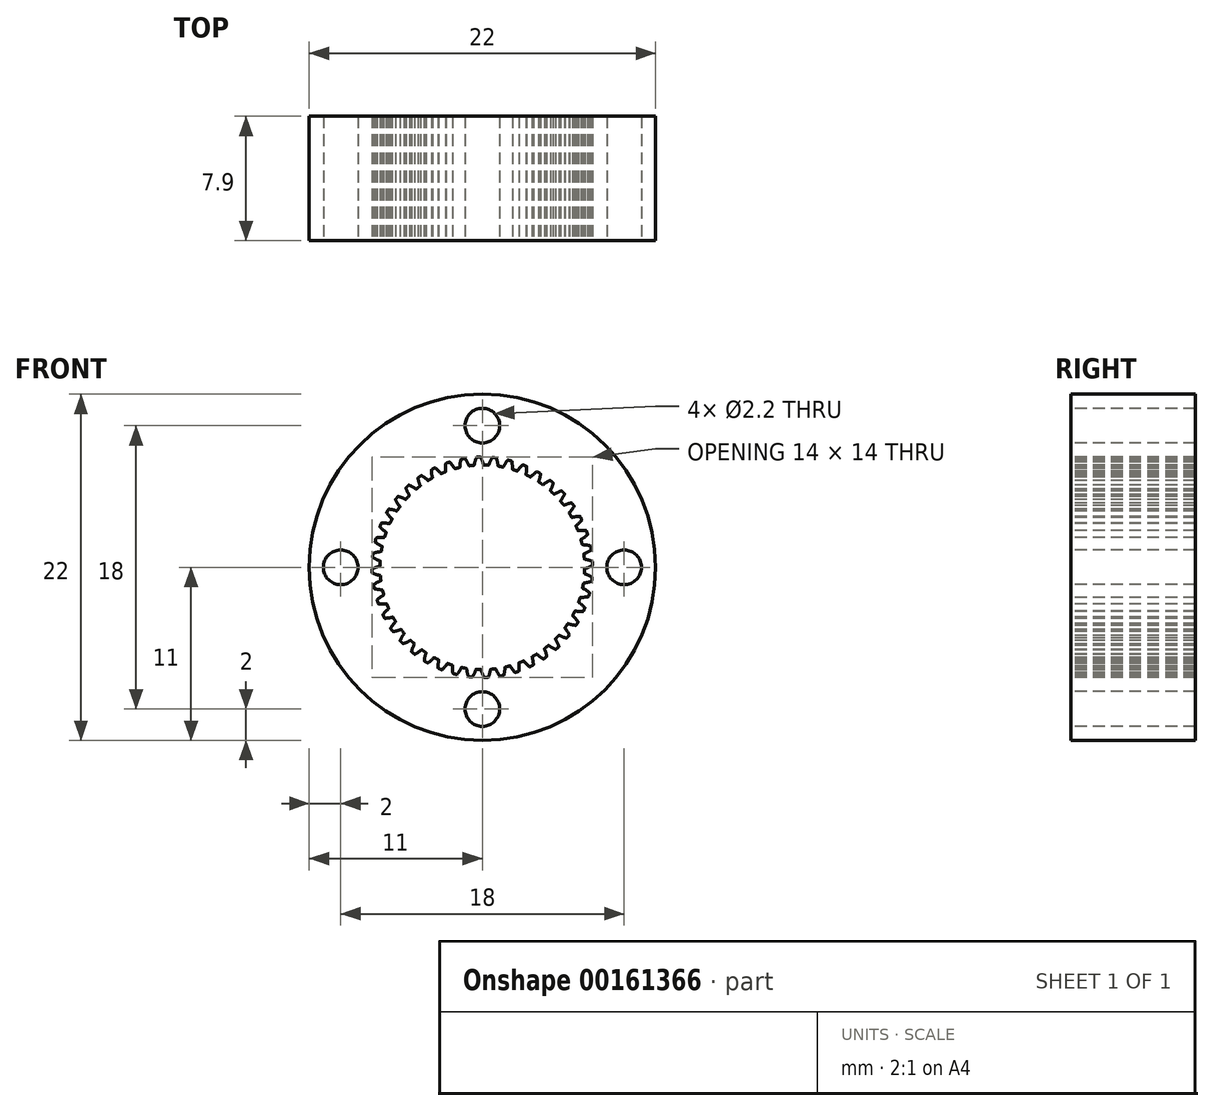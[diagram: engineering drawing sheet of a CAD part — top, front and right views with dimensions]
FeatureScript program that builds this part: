
annotation { "Feature Type Name" : "Feature", "Feature Type Description" : "" }
export const myFeature = defineFeature(function(context is Context, id is Id, definition is map)
    precondition{}
    {
        {
            var Q0;
            Q0=qCreatedBy(makeId("Front.planeOp"),FACE);
            var sketch = newSketch(context, id + "F0", { "sketchPlane" : qUnion([Q0])});
            skCircle(sketch, "E0", {"center": v(0, 0) * mm, "radius": 11 * mm});
            skSolve(sketch);
        }
        {
            var Q0;
            Q0=qSketchRegion(id+"F0",true);
            var Q1;
            Q1=makeQuery(id+"F0.imprint","IMPRINT",FACE,{"disambiguationData":[TD([[makeQuery(id+"F0.imprint","IMPRINT",EDGE,{"derivedFrom":sQuery(id+"F0.wireOp",EDGE,"E0")}),1.0]])]});
            extrude(context, id + "F1", {"entities" : qUnion([Q0, Q1]), "depth" : 7.9 * mm});
        }
        {
            var Q0;
            Q0=makeQuery(id+"F1.opExtrude","CAP_FACE",FACE,{"disambiguationData":[OSD([sQuery(id+"F0.wireOp",EDGE,"E0"),sQuery(id+"F0.wireOp",EDGE,"2902f3af-6cdb-4536-80c8-8346aa25ecb7")])],"isStart":false});
            var sketch = newSketch(context, id + "F2", { "sketchPlane" : qUnion([Q0])});
            skLineSegment(sketch, "E1", {"start": v(0, 27.51) * mm, "end": v(0, -34.9) * mm, "construction": true});
            skCircle(sketch, "E2", {"center": v(0, 9) * mm, "radius": 1.1 * mm});
            skCircle(sketch, "E3.1.0", {"center": v(-9, 0) * mm, "radius": 1.1 * mm});
            skCircle(sketch, "E3.2.0", {"center": v(0, -9) * mm, "radius": 1.1 * mm});
            skCircle(sketch, "E3.3.0", {"center": v(9, 0) * mm, "radius": 1.1 * mm});
            skPoint(sketch, "E3.center", {"position": v(0, 0) * mm});
            skSolve(sketch);
        }
        {
            var Q0;
            Q0=qSketchRegion(id+"F2",true);
            extrude(context, id + "F3", {"entities" : qUnion([Q0]), "operationType" : NewBodyOperationType.REMOVE, "endBound" : BoundingType.THROUGH_ALL, "oppositeDirection" : true, "depth" : 25 * mm});
        }
        {
            var Q0;
            Q0=makeQuery(id+"F1.opExtrude","CAP_FACE",FACE,{"disambiguationData":[OSD([sQuery(id+"F0.wireOp",EDGE,"E0")])],"isStart":false});
            var sketch = newSketch(context, id + "F4", { "sketchPlane" : qUnion([Q0])});
            skCircle(sketch, "E4", {"center": v(0, 0) * mm, "radius": 7 * mm, "construction": true});
            skCircle(sketch, "E5", {"center": v(0, 0) * mm, "radius": 6.75 * mm, "construction": true});
            skCircle(sketch, "E6", {"center": v(0, 0) * mm, "radius": 6.5 * mm, "construction": true});
            skLineSegment(sketch, "E7", {"start": v(0, 0) * mm, "end": v(0, 20.22) * mm, "construction": true});
            skLineSegment(sketch, "E8", {"start": v(0, 0) * mm, "end": v(-0.7, 20.22) * mm, "construction": true});
            skLineSegment(sketch, "E9", {"start": v(0, 6.75) * mm, "end": v(-8.2, 6.75) * mm, "construction": true});
            skLineSegment(sketch, "E10", {"start": v(0, 6.75) * mm, "end": v(-7.4, 4.05) * mm, "construction": true});
            skCircle(sketch, "E11", {"center": v(0, 6.75) * mm, "radius": 2.07 * mm, "construction": true});
            skCircle(sketch, "E12", {"center": v(-1.95, 6.04) * mm, "radius": 2.07 * mm, "construction": true});
            skArc(sketch, "E13", {"start": v(-0.1, 7) * mm, "mid": v(0, 6.76) * mm, "end": v(0.07, 6.5) * mm, "construction": true});
            skArc(sketch, "E14.MirrorCS", {"start": v(-0.37, 7) * mm, "mid": v(-0.46, 6.74) * mm, "end": v(-0.52, 6.48) * mm, "construction": true});
            skArc(sketch, "E15", {"start": v(-0.37, 6.98) * mm, "mid": v(-0.46, 6.74) * mm, "end": v(-0.52, 6.49) * mm});
            skArc(sketch, "E16", {"start": v(-0.36, 7) * mm, "mid": v(-0.24, 7) * mm, "end": v(-0.12, 7) * mm});
            skArc(sketch, "E17", {"start": v(-0.1, 7) * mm, "mid": v(0, 6.76) * mm, "end": v(0.07, 6.5) * mm});
            skArc(sketch, "E18", {"start": v(-0.53, 6.48) * mm, "mid": v(0.22, -6.5) * mm, "end": v(0.08, 6.5) * mm});
            skPoint(sketch, "E19.visualSharp", {"position": v(-0.52, 6.48) * mm});
            skArc(sketch, "E19.filletArc", {"start": v(-0.53, 6.48) * mm, "mid": v(-0.52, 6.48) * mm, "end": v(-0.52, 6.49) * mm});
            skPoint(sketch, "E20.visualSharp", {"position": v(-0.37, 7) * mm});
            skArc(sketch, "E20.filletArc", {"start": v(-0.36, 7) * mm, "mid": v(-0.37, 6.99) * mm, "end": v(-0.37, 6.98) * mm});
            skPoint(sketch, "E21.visualSharp", {"position": v(-0.1, 7) * mm});
            skArc(sketch, "E21.filletArc", {"start": v(-0.1, 7) * mm, "mid": v(-0.11, 7) * mm, "end": v(-0.12, 7) * mm});
            skPoint(sketch, "E22.visualSharp", {"position": v(0.07, 6.5) * mm});
            skArc(sketch, "E22.filletArc", {"start": v(0.07, 6.5) * mm, "mid": v(0.08, 6.5) * mm, "end": v(0.08, 6.5) * mm});
            skArc(sketch, "E23.1.0", {"start": v(-1.44, 6.34) * mm, "mid": v(-1.44, 6.34) * mm, "end": v(-1.43, 6.35) * mm});
            skArc(sketch, "E23.1.1", {"start": v(-1.36, 6.86) * mm, "mid": v(-1.41, 6.6) * mm, "end": v(-1.43, 6.35) * mm});
            skArc(sketch, "E23.1.2", {"start": v(-1.35, 6.87) * mm, "mid": v(-1.36, 6.87) * mm, "end": v(-1.36, 6.86) * mm});
            skArc(sketch, "E23.1.3", {"start": v(-1.35, 6.87) * mm, "mid": v(-1.23, 6.9) * mm, "end": v(-1.11, 6.91) * mm});
            skArc(sketch, "E23.1.4", {"start": v(-1.1, 6.9) * mm, "mid": v(-1.1, 6.91) * mm, "end": v(-1.11, 6.91) * mm});
            skArc(sketch, "E23.1.5", {"start": v(-1.1, 6.9) * mm, "mid": v(-0.96, 6.69) * mm, "end": v(-0.86, 6.45) * mm});
            skArc(sketch, "E23.1.6", {"start": v(-0.86, 6.45) * mm, "mid": v(-0.85, 6.45) * mm, "end": v(-0.84, 6.45) * mm});
            skArc(sketch, "E23.2.0", {"start": v(-2.33, 6.07) * mm, "mid": v(-2.32, 6.07) * mm, "end": v(-2.32, 6.08) * mm});
            skArc(sketch, "E23.2.1", {"start": v(-2.32, 6.6) * mm, "mid": v(-2.34, 6.34) * mm, "end": v(-2.32, 6.08) * mm});
            skArc(sketch, "E23.2.2", {"start": v(-2.31, 6.6) * mm, "mid": v(-2.32, 6.6) * mm, "end": v(-2.32, 6.6) * mm});
            skArc(sketch, "E23.2.3", {"start": v(-2.31, 6.6) * mm, "mid": v(-2.2, 6.65) * mm, "end": v(-2.09, 6.68) * mm});
            skArc(sketch, "E23.2.4", {"start": v(-2.07, 6.68) * mm, "mid": v(-2.08, 6.68) * mm, "end": v(-2.09, 6.68) * mm});
            skArc(sketch, "E23.2.5", {"start": v(-2.07, 6.68) * mm, "mid": v(-1.9, 6.48) * mm, "end": v(-1.77, 6.27) * mm});
            skArc(sketch, "E23.2.6", {"start": v(-1.77, 6.27) * mm, "mid": v(-1.76, 6.26) * mm, "end": v(-1.75, 6.26) * mm});
            skArc(sketch, "E23.3.0", {"start": v(-3.17, 5.67) * mm, "mid": v(-3.17, 5.68) * mm, "end": v(-3.16, 5.69) * mm});
            skArc(sketch, "E23.3.1", {"start": v(-3.24, 6.2) * mm, "mid": v(-3.22, 5.94) * mm, "end": v(-3.16, 5.69) * mm});
            skArc(sketch, "E23.3.2", {"start": v(-3.23, 6.2) * mm, "mid": v(-3.24, 6.2) * mm, "end": v(-3.24, 6.2) * mm});
            skArc(sketch, "E23.3.3", {"start": v(-3.23, 6.2) * mm, "mid": v(-3.12, 6.26) * mm, "end": v(-3.01, 6.32) * mm});
            skArc(sketch, "E23.3.4", {"start": v(-3, 6.32) * mm, "mid": v(-3, 6.32) * mm, "end": v(-3.01, 6.32) * mm});
            skArc(sketch, "E23.3.5", {"start": v(-3, 6.32) * mm, "mid": v(-2.8, 6.14) * mm, "end": v(-2.64, 5.95) * mm});
            skArc(sketch, "E23.3.6", {"start": v(-2.64, 5.95) * mm, "mid": v(-2.63, 5.95) * mm, "end": v(-2.62, 5.95) * mm});
            skArc(sketch, "E23.4.0", {"start": v(-3.95, 5.16) * mm, "mid": v(-3.94, 5.17) * mm, "end": v(-3.94, 5.18) * mm});
            skArc(sketch, "E23.4.1", {"start": v(-4.09, 5.67) * mm, "mid": v(-4.03, 5.42) * mm, "end": v(-3.94, 5.18) * mm});
            skArc(sketch, "E23.4.2", {"start": v(-4.08, 5.69) * mm, "mid": v(-4.09, 5.68) * mm, "end": v(-4.09, 5.67) * mm});
            skArc(sketch, "E23.4.3", {"start": v(-4.08, 5.69) * mm, "mid": v(-3.98, 5.76) * mm, "end": v(-3.88, 5.82) * mm});
            skArc(sketch, "E23.4.4", {"start": v(-3.87, 5.82) * mm, "mid": v(-3.88, 5.83) * mm, "end": v(-3.88, 5.82) * mm});
            skArc(sketch, "E23.4.5", {"start": v(-3.87, 5.82) * mm, "mid": v(-3.65, 5.68) * mm, "end": v(-3.46, 5.52) * mm});
            skArc(sketch, "E23.4.6", {"start": v(-3.46, 5.52) * mm, "mid": v(-3.45, 5.51) * mm, "end": v(-3.44, 5.51) * mm});
            skArc(sketch, "E23.5.0", {"start": v(-4.64, 4.55) * mm, "mid": v(-4.64, 4.56) * mm, "end": v(-4.64, 4.57) * mm});
            skArc(sketch, "E23.5.1", {"start": v(-4.85, 5.03) * mm, "mid": v(-4.76, 4.8) * mm, "end": v(-4.64, 4.57) * mm});
            skArc(sketch, "E23.5.2", {"start": v(-4.85, 5.05) * mm, "mid": v(-4.85, 5.04) * mm, "end": v(-4.85, 5.03) * mm});
            skArc(sketch, "E23.5.3", {"start": v(-4.85, 5.05) * mm, "mid": v(-4.76, 5.13) * mm, "end": v(-4.67, 5.21) * mm});
            skArc(sketch, "E23.5.4", {"start": v(-4.66, 5.21) * mm, "mid": v(-4.67, 5.22) * mm, "end": v(-4.67, 5.21) * mm});
            skArc(sketch, "E23.5.5", {"start": v(-4.66, 5.21) * mm, "mid": v(-4.43, 5.1) * mm, "end": v(-4.2, 4.97) * mm});
            skArc(sketch, "E23.5.6", {"start": v(-4.2, 4.97) * mm, "mid": v(-4.2, 4.96) * mm, "end": v(-4.2, 4.97) * mm});
            skArc(sketch, "E23.6.0", {"start": v(-5.24, 3.84) * mm, "mid": v(-5.24, 3.85) * mm, "end": v(-5.24, 3.86) * mm});
            skArc(sketch, "E23.6.1", {"start": v(-5.52, 4.3) * mm, "mid": v(-5.4, 4.07) * mm, "end": v(-5.24, 3.86) * mm});
            skArc(sketch, "E23.6.2", {"start": v(-5.52, 4.3) * mm, "mid": v(-5.52, 4.3) * mm, "end": v(-5.52, 4.3) * mm});
            skArc(sketch, "E23.6.3", {"start": v(-5.52, 4.3) * mm, "mid": v(-5.44, 4.4) * mm, "end": v(-5.37, 4.5) * mm});
            skArc(sketch, "E23.6.4", {"start": v(-5.35, 4.5) * mm, "mid": v(-5.36, 4.5) * mm, "end": v(-5.37, 4.5) * mm});
            skArc(sketch, "E23.6.5", {"start": v(-5.35, 4.5) * mm, "mid": v(-5.1, 4.42) * mm, "end": v(-4.87, 4.32) * mm});
            skArc(sketch, "E23.6.6", {"start": v(-4.87, 4.32) * mm, "mid": v(-4.86, 4.32) * mm, "end": v(-4.86, 4.32) * mm});
            skArc(sketch, "E23.7.0", {"start": v(-5.74, 3.06) * mm, "mid": v(-5.73, 3.07) * mm, "end": v(-5.74, 3.08) * mm});
            skArc(sketch, "E23.7.1", {"start": v(-6.08, 3.46) * mm, "mid": v(-5.92, 3.26) * mm, "end": v(-5.74, 3.08) * mm});
            skArc(sketch, "E23.7.2", {"start": v(-6.08, 3.48) * mm, "mid": v(-6.08, 3.47) * mm, "end": v(-6.08, 3.46) * mm});
            skArc(sketch, "E23.7.3", {"start": v(-6.08, 3.48) * mm, "mid": v(-6.01, 3.58) * mm, "end": v(-5.95, 3.68) * mm});
            skArc(sketch, "E23.7.4", {"start": v(-5.94, 3.7) * mm, "mid": v(-5.95, 3.69) * mm, "end": v(-5.95, 3.68) * mm});
            skArc(sketch, "E23.7.5", {"start": v(-5.94, 3.7) * mm, "mid": v(-5.69, 3.65) * mm, "end": v(-5.44, 3.58) * mm});
            skArc(sketch, "E23.7.6", {"start": v(-5.44, 3.58) * mm, "mid": v(-5.43, 3.58) * mm, "end": v(-5.42, 3.58) * mm});
            skArc(sketch, "E23.8.0", {"start": v(-6.11, 2.21) * mm, "mid": v(-6.11, 2.22) * mm, "end": v(-6.12, 2.23) * mm});
            skArc(sketch, "E23.8.1", {"start": v(-6.5, 2.56) * mm, "mid": v(-6.32, 2.38) * mm, "end": v(-6.12, 2.23) * mm});
            skArc(sketch, "E23.8.2", {"start": v(-6.5, 2.58) * mm, "mid": v(-6.5, 2.57) * mm, "end": v(-6.5, 2.56) * mm});
            skArc(sketch, "E23.8.3", {"start": v(-6.5, 2.58) * mm, "mid": v(-6.46, 2.69) * mm, "end": v(-6.42, 2.8) * mm});
            skArc(sketch, "E23.8.4", {"start": v(-6.4, 2.8) * mm, "mid": v(-6.41, 2.8) * mm, "end": v(-6.42, 2.8) * mm});
            skArc(sketch, "E23.8.5", {"start": v(-6.4, 2.8) * mm, "mid": v(-6.15, 2.8) * mm, "end": v(-5.9, 2.77) * mm});
            skArc(sketch, "E23.8.6", {"start": v(-5.9, 2.77) * mm, "mid": v(-5.88, 2.77) * mm, "end": v(-5.88, 2.78) * mm});
            skArc(sketch, "E23.9.0", {"start": v(-6.36, 1.32) * mm, "mid": v(-6.37, 1.33) * mm, "end": v(-6.37, 1.33) * mm});
            skArc(sketch, "E23.9.1", {"start": v(-6.8, 1.61) * mm, "mid": v(-6.6, 1.46) * mm, "end": v(-6.37, 1.33) * mm});
            skArc(sketch, "E23.9.2", {"start": v(-6.8, 1.62) * mm, "mid": v(-6.8, 1.62) * mm, "end": v(-6.8, 1.61) * mm});
            skArc(sketch, "E23.9.3", {"start": v(-6.8, 1.62) * mm, "mid": v(-6.78, 1.74) * mm, "end": v(-6.75, 1.86) * mm});
            skArc(sketch, "E23.9.4", {"start": v(-6.74, 1.87) * mm, "mid": v(-6.74, 1.86) * mm, "end": v(-6.75, 1.86) * mm});
            skArc(sketch, "E23.9.5", {"start": v(-6.74, 1.87) * mm, "mid": v(-6.48, 1.9) * mm, "end": v(-6.23, 1.9) * mm});
            skArc(sketch, "E23.9.6", {"start": v(-6.23, 1.9) * mm, "mid": v(-6.22, 1.9) * mm, "end": v(-6.21, 1.91) * mm});
            skArc(sketch, "E23.10.0", {"start": v(-6.49, 0.4) * mm, "mid": v(-6.5, 0.4) * mm, "end": v(-6.5, 0.41) * mm});
            skArc(sketch, "E23.10.1", {"start": v(-6.96, 0.63) * mm, "mid": v(-6.74, 0.5) * mm, "end": v(-6.5, 0.41) * mm});
            skArc(sketch, "E23.10.2", {"start": v(-6.97, 0.64) * mm, "mid": v(-6.97, 0.63) * mm, "end": v(-6.96, 0.63) * mm});
            skArc(sketch, "E23.10.3", {"start": v(-6.97, 0.64) * mm, "mid": v(-6.96, 0.76) * mm, "end": v(-6.94, 0.88) * mm});
            skArc(sketch, "E23.10.4", {"start": v(-6.94, 0.9) * mm, "mid": v(-6.94, 0.89) * mm, "end": v(-6.94, 0.88) * mm});
            skArc(sketch, "E23.10.5", {"start": v(-6.94, 0.9) * mm, "mid": v(-6.69, 0.96) * mm, "end": v(-6.43, 1) * mm});
            skArc(sketch, "E23.10.6", {"start": v(-6.43, 1) * mm, "mid": v(-6.43, 1) * mm, "end": v(-6.42, 1) * mm});
            skArc(sketch, "E23.11.0", {"start": v(-6.48, -0.53) * mm, "mid": v(-6.48, -0.52) * mm, "end": v(-6.49, -0.52) * mm});
            skArc(sketch, "E23.11.1", {"start": v(-6.98, -0.37) * mm, "mid": v(-6.74, -0.46) * mm, "end": v(-6.49, -0.52) * mm});
            skArc(sketch, "E23.11.2", {"start": v(-7, -0.36) * mm, "mid": v(-6.99, -0.37) * mm, "end": v(-6.98, -0.37) * mm});
            skArc(sketch, "E23.11.3", {"start": v(-7, -0.36) * mm, "mid": v(-7, -0.24) * mm, "end": v(-7, -0.12) * mm});
            skArc(sketch, "E23.11.4", {"start": v(-7, -0.1) * mm, "mid": v(-7, -0.11) * mm, "end": v(-7, -0.12) * mm});
            skArc(sketch, "E23.11.5", {"start": v(-7, -0.1) * mm, "mid": v(-6.76, 0) * mm, "end": v(-6.5, 0.07) * mm});
            skArc(sketch, "E23.11.6", {"start": v(-6.5, 0.07) * mm, "mid": v(-6.5, 0.08) * mm, "end": v(-6.5, 0.08) * mm});
            skArc(sketch, "E23.12.0", {"start": v(-6.34, -1.44) * mm, "mid": v(-6.34, -1.44) * mm, "end": v(-6.35, -1.43) * mm});
            skArc(sketch, "E23.12.1", {"start": v(-6.86, -1.36) * mm, "mid": v(-6.6, -1.41) * mm, "end": v(-6.35, -1.43) * mm});
            skArc(sketch, "E23.12.2", {"start": v(-6.87, -1.35) * mm, "mid": v(-6.87, -1.36) * mm, "end": v(-6.86, -1.36) * mm});
            skArc(sketch, "E23.12.3", {"start": v(-6.87, -1.35) * mm, "mid": v(-6.9, -1.23) * mm, "end": v(-6.91, -1.11) * mm});
            skArc(sketch, "E23.12.4", {"start": v(-6.9, -1.1) * mm, "mid": v(-6.91, -1.1) * mm, "end": v(-6.91, -1.11) * mm});
            skArc(sketch, "E23.12.5", {"start": v(-6.9, -1.1) * mm, "mid": v(-6.69, -0.96) * mm, "end": v(-6.45, -0.86) * mm});
            skArc(sketch, "E23.12.6", {"start": v(-6.45, -0.86) * mm, "mid": v(-6.45, -0.85) * mm, "end": v(-6.45, -0.84) * mm});
            skArc(sketch, "E23.13.0", {"start": v(-6.07, -2.33) * mm, "mid": v(-6.07, -2.32) * mm, "end": v(-6.08, -2.32) * mm});
            skArc(sketch, "E23.13.1", {"start": v(-6.6, -2.32) * mm, "mid": v(-6.34, -2.34) * mm, "end": v(-6.08, -2.32) * mm});
            skArc(sketch, "E23.13.2", {"start": v(-6.6, -2.31) * mm, "mid": v(-6.6, -2.32) * mm, "end": v(-6.6, -2.32) * mm});
            skArc(sketch, "E23.13.3", {"start": v(-6.6, -2.31) * mm, "mid": v(-6.65, -2.2) * mm, "end": v(-6.68, -2.09) * mm});
            skArc(sketch, "E23.13.4", {"start": v(-6.68, -2.07) * mm, "mid": v(-6.68, -2.08) * mm, "end": v(-6.68, -2.09) * mm});
            skArc(sketch, "E23.13.5", {"start": v(-6.68, -2.07) * mm, "mid": v(-6.48, -1.9) * mm, "end": v(-6.27, -1.77) * mm});
            skArc(sketch, "E23.13.6", {"start": v(-6.27, -1.77) * mm, "mid": v(-6.26, -1.76) * mm, "end": v(-6.26, -1.75) * mm});
            skArc(sketch, "E23.14.0", {"start": v(-5.67, -3.17) * mm, "mid": v(-5.68, -3.17) * mm, "end": v(-5.69, -3.16) * mm});
            skArc(sketch, "E23.14.1", {"start": v(-6.2, -3.24) * mm, "mid": v(-5.94, -3.22) * mm, "end": v(-5.69, -3.16) * mm});
            skArc(sketch, "E23.14.2", {"start": v(-6.2, -3.23) * mm, "mid": v(-6.2, -3.24) * mm, "end": v(-6.2, -3.24) * mm});
            skArc(sketch, "E23.14.3", {"start": v(-6.2, -3.23) * mm, "mid": v(-6.26, -3.12) * mm, "end": v(-6.32, -3.01) * mm});
            skArc(sketch, "E23.14.4", {"start": v(-6.32, -3) * mm, "mid": v(-6.32, -3) * mm, "end": v(-6.32, -3.01) * mm});
            skArc(sketch, "E23.14.5", {"start": v(-6.32, -3) * mm, "mid": v(-6.14, -2.8) * mm, "end": v(-5.95, -2.64) * mm});
            skArc(sketch, "E23.14.6", {"start": v(-5.95, -2.64) * mm, "mid": v(-5.95, -2.63) * mm, "end": v(-5.95, -2.62) * mm});
            skArc(sketch, "E23.15.0", {"start": v(-5.16, -3.95) * mm, "mid": v(-5.17, -3.94) * mm, "end": v(-5.18, -3.94) * mm});
            skArc(sketch, "E23.15.1", {"start": v(-5.67, -4.09) * mm, "mid": v(-5.42, -4.03) * mm, "end": v(-5.18, -3.94) * mm});
            skArc(sketch, "E23.15.2", {"start": v(-5.69, -4.08) * mm, "mid": v(-5.68, -4.09) * mm, "end": v(-5.67, -4.09) * mm});
            skArc(sketch, "E23.15.3", {"start": v(-5.69, -4.08) * mm, "mid": v(-5.76, -3.98) * mm, "end": v(-5.82, -3.88) * mm});
            skArc(sketch, "E23.15.4", {"start": v(-5.82, -3.87) * mm, "mid": v(-5.83, -3.88) * mm, "end": v(-5.82, -3.88) * mm});
            skArc(sketch, "E23.15.5", {"start": v(-5.82, -3.87) * mm, "mid": v(-5.68, -3.65) * mm, "end": v(-5.52, -3.46) * mm});
            skArc(sketch, "E23.15.6", {"start": v(-5.52, -3.46) * mm, "mid": v(-5.51, -3.45) * mm, "end": v(-5.51, -3.44) * mm});
            skArc(sketch, "E23.16.0", {"start": v(-4.55, -4.64) * mm, "mid": v(-4.56, -4.64) * mm, "end": v(-4.57, -4.64) * mm});
            skArc(sketch, "E23.16.1", {"start": v(-5.03, -4.85) * mm, "mid": v(-4.8, -4.76) * mm, "end": v(-4.57, -4.64) * mm});
            skArc(sketch, "E23.16.2", {"start": v(-5.05, -4.85) * mm, "mid": v(-5.04, -4.85) * mm, "end": v(-5.03, -4.85) * mm});
            skArc(sketch, "E23.16.3", {"start": v(-5.05, -4.85) * mm, "mid": v(-5.13, -4.76) * mm, "end": v(-5.21, -4.67) * mm});
            skArc(sketch, "E23.16.4", {"start": v(-5.21, -4.66) * mm, "mid": v(-5.22, -4.67) * mm, "end": v(-5.21, -4.67) * mm});
            skArc(sketch, "E23.16.5", {"start": v(-5.21, -4.66) * mm, "mid": v(-5.1, -4.43) * mm, "end": v(-4.97, -4.2) * mm});
            skArc(sketch, "E23.16.6", {"start": v(-4.97, -4.2) * mm, "mid": v(-4.96, -4.2) * mm, "end": v(-4.97, -4.2) * mm});
            skArc(sketch, "E23.17.0", {"start": v(-3.84, -5.24) * mm, "mid": v(-3.85, -5.24) * mm, "end": v(-3.86, -5.24) * mm});
            skArc(sketch, "E23.17.1", {"start": v(-4.3, -5.52) * mm, "mid": v(-4.07, -5.4) * mm, "end": v(-3.86, -5.24) * mm});
            skArc(sketch, "E23.17.2", {"start": v(-4.3, -5.52) * mm, "mid": v(-4.3, -5.52) * mm, "end": v(-4.3, -5.52) * mm});
            skArc(sketch, "E23.17.3", {"start": v(-4.3, -5.52) * mm, "mid": v(-4.4, -5.44) * mm, "end": v(-4.5, -5.37) * mm});
            skArc(sketch, "E23.17.4", {"start": v(-4.5, -5.35) * mm, "mid": v(-4.5, -5.36) * mm, "end": v(-4.5, -5.37) * mm});
            skArc(sketch, "E23.17.5", {"start": v(-4.5, -5.35) * mm, "mid": v(-4.42, -5.1) * mm, "end": v(-4.32, -4.87) * mm});
            skArc(sketch, "E23.17.6", {"start": v(-4.32, -4.87) * mm, "mid": v(-4.32, -4.86) * mm, "end": v(-4.32, -4.86) * mm});
            skArc(sketch, "E23.18.0", {"start": v(-3.06, -5.74) * mm, "mid": v(-3.07, -5.73) * mm, "end": v(-3.08, -5.74) * mm});
            skArc(sketch, "E23.18.1", {"start": v(-3.46, -6.08) * mm, "mid": v(-3.26, -5.92) * mm, "end": v(-3.08, -5.74) * mm});
            skArc(sketch, "E23.18.2", {"start": v(-3.48, -6.08) * mm, "mid": v(-3.47, -6.08) * mm, "end": v(-3.46, -6.08) * mm});
            skArc(sketch, "E23.18.3", {"start": v(-3.48, -6.08) * mm, "mid": v(-3.58, -6.01) * mm, "end": v(-3.68, -5.95) * mm});
            skArc(sketch, "E23.18.4", {"start": v(-3.7, -5.94) * mm, "mid": v(-3.69, -5.95) * mm, "end": v(-3.68, -5.95) * mm});
            skArc(sketch, "E23.18.5", {"start": v(-3.7, -5.94) * mm, "mid": v(-3.65, -5.69) * mm, "end": v(-3.58, -5.44) * mm});
            skArc(sketch, "E23.18.6", {"start": v(-3.58, -5.44) * mm, "mid": v(-3.58, -5.43) * mm, "end": v(-3.58, -5.42) * mm});
            skArc(sketch, "E23.19.0", {"start": v(-2.21, -6.11) * mm, "mid": v(-2.22, -6.11) * mm, "end": v(-2.23, -6.12) * mm});
            skArc(sketch, "E23.19.1", {"start": v(-2.56, -6.5) * mm, "mid": v(-2.38, -6.32) * mm, "end": v(-2.23, -6.12) * mm});
            skArc(sketch, "E23.19.2", {"start": v(-2.58, -6.5) * mm, "mid": v(-2.57, -6.5) * mm, "end": v(-2.56, -6.5) * mm});
            skArc(sketch, "E23.19.3", {"start": v(-2.58, -6.5) * mm, "mid": v(-2.69, -6.46) * mm, "end": v(-2.8, -6.42) * mm});
            skArc(sketch, "E23.19.4", {"start": v(-2.8, -6.4) * mm, "mid": v(-2.8, -6.41) * mm, "end": v(-2.8, -6.42) * mm});
            skArc(sketch, "E23.19.5", {"start": v(-2.8, -6.4) * mm, "mid": v(-2.8, -6.15) * mm, "end": v(-2.77, -5.9) * mm});
            skArc(sketch, "E23.19.6", {"start": v(-2.77, -5.9) * mm, "mid": v(-2.77, -5.88) * mm, "end": v(-2.78, -5.88) * mm});
            skArc(sketch, "E23.20.0", {"start": v(-1.32, -6.36) * mm, "mid": v(-1.33, -6.37) * mm, "end": v(-1.33, -6.37) * mm});
            skArc(sketch, "E23.20.1", {"start": v(-1.61, -6.8) * mm, "mid": v(-1.46, -6.6) * mm, "end": v(-1.33, -6.37) * mm});
            skArc(sketch, "E23.20.2", {"start": v(-1.62, -6.8) * mm, "mid": v(-1.62, -6.8) * mm, "end": v(-1.61, -6.8) * mm});
            skArc(sketch, "E23.20.3", {"start": v(-1.62, -6.8) * mm, "mid": v(-1.74, -6.78) * mm, "end": v(-1.86, -6.75) * mm});
            skArc(sketch, "E23.20.4", {"start": v(-1.87, -6.74) * mm, "mid": v(-1.86, -6.74) * mm, "end": v(-1.86, -6.75) * mm});
            skArc(sketch, "E23.20.5", {"start": v(-1.87, -6.74) * mm, "mid": v(-1.9, -6.48) * mm, "end": v(-1.9, -6.23) * mm});
            skArc(sketch, "E23.20.6", {"start": v(-1.9, -6.23) * mm, "mid": v(-1.9, -6.22) * mm, "end": v(-1.91, -6.21) * mm});
            skArc(sketch, "E23.21.0", {"start": v(-0.4, -6.49) * mm, "mid": v(-0.4, -6.5) * mm, "end": v(-0.41, -6.5) * mm});
            skArc(sketch, "E23.21.1", {"start": v(-0.63, -6.96) * mm, "mid": v(-0.5, -6.74) * mm, "end": v(-0.41, -6.5) * mm});
            skArc(sketch, "E23.21.2", {"start": v(-0.64, -6.97) * mm, "mid": v(-0.63, -6.97) * mm, "end": v(-0.63, -6.96) * mm});
            skArc(sketch, "E23.21.3", {"start": v(-0.64, -6.97) * mm, "mid": v(-0.76, -6.96) * mm, "end": v(-0.88, -6.94) * mm});
            skArc(sketch, "E23.21.4", {"start": v(-0.9, -6.94) * mm, "mid": v(-0.89, -6.94) * mm, "end": v(-0.88, -6.94) * mm});
            skArc(sketch, "E23.21.5", {"start": v(-0.9, -6.94) * mm, "mid": v(-0.96, -6.69) * mm, "end": v(-1, -6.43) * mm});
            skArc(sketch, "E23.21.6", {"start": v(-1, -6.43) * mm, "mid": v(-1, -6.43) * mm, "end": v(-1, -6.42) * mm});
            skArc(sketch, "E23.22.0", {"start": v(0.53, -6.48) * mm, "mid": v(0.52, -6.48) * mm, "end": v(0.52, -6.49) * mm});
            skArc(sketch, "E23.22.1", {"start": v(0.37, -6.98) * mm, "mid": v(0.46, -6.74) * mm, "end": v(0.52, -6.49) * mm});
            skArc(sketch, "E23.22.2", {"start": v(0.36, -7) * mm, "mid": v(0.37, -6.99) * mm, "end": v(0.37, -6.98) * mm});
            skArc(sketch, "E23.22.3", {"start": v(0.36, -7) * mm, "mid": v(0.24, -7) * mm, "end": v(0.12, -7) * mm});
            skArc(sketch, "E23.22.4", {"start": v(0.1, -7) * mm, "mid": v(0.11, -7) * mm, "end": v(0.12, -7) * mm});
            skArc(sketch, "E23.22.5", {"start": v(0.1, -7) * mm, "mid": v(0, -6.76) * mm, "end": v(-0.07, -6.5) * mm});
            skArc(sketch, "E23.22.6", {"start": v(-0.07, -6.5) * mm, "mid": v(-0.08, -6.5) * mm, "end": v(-0.08, -6.5) * mm});
            skArc(sketch, "E23.23.0", {"start": v(1.44, -6.34) * mm, "mid": v(1.44, -6.34) * mm, "end": v(1.43, -6.35) * mm});
            skArc(sketch, "E23.23.1", {"start": v(1.36, -6.86) * mm, "mid": v(1.41, -6.6) * mm, "end": v(1.43, -6.35) * mm});
            skArc(sketch, "E23.23.2", {"start": v(1.35, -6.87) * mm, "mid": v(1.36, -6.87) * mm, "end": v(1.36, -6.86) * mm});
            skArc(sketch, "E23.23.3", {"start": v(1.35, -6.87) * mm, "mid": v(1.23, -6.9) * mm, "end": v(1.11, -6.91) * mm});
            skArc(sketch, "E23.23.4", {"start": v(1.1, -6.9) * mm, "mid": v(1.1, -6.91) * mm, "end": v(1.11, -6.91) * mm});
            skArc(sketch, "E23.23.5", {"start": v(1.1, -6.9) * mm, "mid": v(0.96, -6.69) * mm, "end": v(0.86, -6.45) * mm});
            skArc(sketch, "E23.23.6", {"start": v(0.86, -6.45) * mm, "mid": v(0.85, -6.45) * mm, "end": v(0.84, -6.45) * mm});
            skArc(sketch, "E23.24.0", {"start": v(2.33, -6.07) * mm, "mid": v(2.32, -6.07) * mm, "end": v(2.32, -6.08) * mm});
            skArc(sketch, "E23.24.1", {"start": v(2.32, -6.6) * mm, "mid": v(2.34, -6.34) * mm, "end": v(2.32, -6.08) * mm});
            skArc(sketch, "E23.24.2", {"start": v(2.31, -6.6) * mm, "mid": v(2.32, -6.6) * mm, "end": v(2.32, -6.6) * mm});
            skArc(sketch, "E23.24.3", {"start": v(2.31, -6.6) * mm, "mid": v(2.2, -6.65) * mm, "end": v(2.09, -6.68) * mm});
            skArc(sketch, "E23.24.4", {"start": v(2.07, -6.68) * mm, "mid": v(2.08, -6.68) * mm, "end": v(2.09, -6.68) * mm});
            skArc(sketch, "E23.24.5", {"start": v(2.07, -6.68) * mm, "mid": v(1.9, -6.48) * mm, "end": v(1.77, -6.27) * mm});
            skArc(sketch, "E23.24.6", {"start": v(1.77, -6.27) * mm, "mid": v(1.76, -6.26) * mm, "end": v(1.75, -6.26) * mm});
            skArc(sketch, "E23.25.0", {"start": v(3.17, -5.67) * mm, "mid": v(3.17, -5.68) * mm, "end": v(3.16, -5.69) * mm});
            skArc(sketch, "E23.25.1", {"start": v(3.24, -6.2) * mm, "mid": v(3.22, -5.94) * mm, "end": v(3.16, -5.69) * mm});
            skArc(sketch, "E23.25.2", {"start": v(3.23, -6.2) * mm, "mid": v(3.24, -6.2) * mm, "end": v(3.24, -6.2) * mm});
            skArc(sketch, "E23.25.3", {"start": v(3.23, -6.2) * mm, "mid": v(3.12, -6.26) * mm, "end": v(3.01, -6.32) * mm});
            skArc(sketch, "E23.25.4", {"start": v(3, -6.32) * mm, "mid": v(3, -6.32) * mm, "end": v(3.01, -6.32) * mm});
            skArc(sketch, "E23.25.5", {"start": v(3, -6.32) * mm, "mid": v(2.8, -6.14) * mm, "end": v(2.64, -5.95) * mm});
            skArc(sketch, "E23.25.6", {"start": v(2.64, -5.95) * mm, "mid": v(2.63, -5.95) * mm, "end": v(2.62, -5.95) * mm});
            skArc(sketch, "E23.26.0", {"start": v(3.95, -5.16) * mm, "mid": v(3.94, -5.17) * mm, "end": v(3.94, -5.18) * mm});
            skArc(sketch, "E23.26.1", {"start": v(4.09, -5.67) * mm, "mid": v(4.03, -5.42) * mm, "end": v(3.94, -5.18) * mm});
            skArc(sketch, "E23.26.2", {"start": v(4.08, -5.69) * mm, "mid": v(4.09, -5.68) * mm, "end": v(4.09, -5.67) * mm});
            skArc(sketch, "E23.26.3", {"start": v(4.08, -5.69) * mm, "mid": v(3.98, -5.76) * mm, "end": v(3.88, -5.82) * mm});
            skArc(sketch, "E23.26.4", {"start": v(3.87, -5.82) * mm, "mid": v(3.88, -5.83) * mm, "end": v(3.88, -5.82) * mm});
            skArc(sketch, "E23.26.5", {"start": v(3.87, -5.82) * mm, "mid": v(3.65, -5.68) * mm, "end": v(3.46, -5.52) * mm});
            skArc(sketch, "E23.26.6", {"start": v(3.46, -5.52) * mm, "mid": v(3.45, -5.51) * mm, "end": v(3.44, -5.51) * mm});
            skArc(sketch, "E23.27.0", {"start": v(4.64, -4.55) * mm, "mid": v(4.64, -4.56) * mm, "end": v(4.64, -4.57) * mm});
            skArc(sketch, "E23.27.1", {"start": v(4.85, -5.03) * mm, "mid": v(4.76, -4.8) * mm, "end": v(4.64, -4.57) * mm});
            skArc(sketch, "E23.27.2", {"start": v(4.85, -5.05) * mm, "mid": v(4.85, -5.04) * mm, "end": v(4.85, -5.03) * mm});
            skArc(sketch, "E23.27.3", {"start": v(4.85, -5.05) * mm, "mid": v(4.76, -5.13) * mm, "end": v(4.67, -5.21) * mm});
            skArc(sketch, "E23.27.4", {"start": v(4.66, -5.21) * mm, "mid": v(4.67, -5.22) * mm, "end": v(4.67, -5.21) * mm});
            skArc(sketch, "E23.27.5", {"start": v(4.66, -5.21) * mm, "mid": v(4.43, -5.1) * mm, "end": v(4.2, -4.97) * mm});
            skArc(sketch, "E23.27.6", {"start": v(4.2, -4.97) * mm, "mid": v(4.2, -4.96) * mm, "end": v(4.2, -4.97) * mm});
            skArc(sketch, "E23.28.0", {"start": v(5.24, -3.84) * mm, "mid": v(5.24, -3.85) * mm, "end": v(5.24, -3.86) * mm});
            skArc(sketch, "E23.28.1", {"start": v(5.52, -4.3) * mm, "mid": v(5.4, -4.07) * mm, "end": v(5.24, -3.86) * mm});
            skArc(sketch, "E23.28.2", {"start": v(5.52, -4.3) * mm, "mid": v(5.52, -4.3) * mm, "end": v(5.52, -4.3) * mm});
            skArc(sketch, "E23.28.3", {"start": v(5.52, -4.3) * mm, "mid": v(5.44, -4.4) * mm, "end": v(5.37, -4.5) * mm});
            skArc(sketch, "E23.28.4", {"start": v(5.35, -4.5) * mm, "mid": v(5.36, -4.5) * mm, "end": v(5.37, -4.5) * mm});
            skArc(sketch, "E23.28.5", {"start": v(5.35, -4.5) * mm, "mid": v(5.1, -4.42) * mm, "end": v(4.87, -4.32) * mm});
            skArc(sketch, "E23.28.6", {"start": v(4.87, -4.32) * mm, "mid": v(4.86, -4.32) * mm, "end": v(4.86, -4.32) * mm});
            skArc(sketch, "E23.29.0", {"start": v(5.74, -3.06) * mm, "mid": v(5.73, -3.07) * mm, "end": v(5.74, -3.08) * mm});
            skArc(sketch, "E23.29.1", {"start": v(6.08, -3.46) * mm, "mid": v(5.92, -3.26) * mm, "end": v(5.74, -3.08) * mm});
            skArc(sketch, "E23.29.2", {"start": v(6.08, -3.48) * mm, "mid": v(6.08, -3.47) * mm, "end": v(6.08, -3.46) * mm});
            skArc(sketch, "E23.29.3", {"start": v(6.08, -3.48) * mm, "mid": v(6.01, -3.58) * mm, "end": v(5.95, -3.68) * mm});
            skArc(sketch, "E23.29.4", {"start": v(5.94, -3.7) * mm, "mid": v(5.95, -3.69) * mm, "end": v(5.95, -3.68) * mm});
            skArc(sketch, "E23.29.5", {"start": v(5.94, -3.7) * mm, "mid": v(5.69, -3.65) * mm, "end": v(5.44, -3.58) * mm});
            skArc(sketch, "E23.29.6", {"start": v(5.44, -3.58) * mm, "mid": v(5.43, -3.58) * mm, "end": v(5.42, -3.58) * mm});
            skArc(sketch, "E23.30.0", {"start": v(6.11, -2.21) * mm, "mid": v(6.11, -2.22) * mm, "end": v(6.12, -2.23) * mm});
            skArc(sketch, "E23.30.1", {"start": v(6.5, -2.56) * mm, "mid": v(6.32, -2.38) * mm, "end": v(6.12, -2.23) * mm});
            skArc(sketch, "E23.30.2", {"start": v(6.5, -2.58) * mm, "mid": v(6.5, -2.57) * mm, "end": v(6.5, -2.56) * mm});
            skArc(sketch, "E23.30.3", {"start": v(6.5, -2.58) * mm, "mid": v(6.46, -2.69) * mm, "end": v(6.42, -2.8) * mm});
            skArc(sketch, "E23.30.4", {"start": v(6.4, -2.8) * mm, "mid": v(6.41, -2.8) * mm, "end": v(6.42, -2.8) * mm});
            skArc(sketch, "E23.30.5", {"start": v(6.4, -2.8) * mm, "mid": v(6.15, -2.8) * mm, "end": v(5.9, -2.77) * mm});
            skArc(sketch, "E23.30.6", {"start": v(5.9, -2.77) * mm, "mid": v(5.88, -2.77) * mm, "end": v(5.88, -2.78) * mm});
            skArc(sketch, "E23.31.0", {"start": v(6.36, -1.32) * mm, "mid": v(6.37, -1.33) * mm, "end": v(6.37, -1.33) * mm});
            skArc(sketch, "E23.31.1", {"start": v(6.8, -1.61) * mm, "mid": v(6.6, -1.46) * mm, "end": v(6.37, -1.33) * mm});
            skArc(sketch, "E23.31.2", {"start": v(6.8, -1.62) * mm, "mid": v(6.8, -1.62) * mm, "end": v(6.8, -1.61) * mm});
            skArc(sketch, "E23.31.3", {"start": v(6.8, -1.62) * mm, "mid": v(6.78, -1.74) * mm, "end": v(6.75, -1.86) * mm});
            skArc(sketch, "E23.31.4", {"start": v(6.74, -1.87) * mm, "mid": v(6.74, -1.86) * mm, "end": v(6.75, -1.86) * mm});
            skArc(sketch, "E23.31.5", {"start": v(6.74, -1.87) * mm, "mid": v(6.48, -1.9) * mm, "end": v(6.23, -1.9) * mm});
            skArc(sketch, "E23.31.6", {"start": v(6.23, -1.9) * mm, "mid": v(6.22, -1.9) * mm, "end": v(6.21, -1.91) * mm});
            skArc(sketch, "E23.32.0", {"start": v(6.49, -0.4) * mm, "mid": v(6.5, -0.4) * mm, "end": v(6.5, -0.41) * mm});
            skArc(sketch, "E23.32.1", {"start": v(6.96, -0.63) * mm, "mid": v(6.74, -0.5) * mm, "end": v(6.5, -0.41) * mm});
            skArc(sketch, "E23.32.2", {"start": v(6.97, -0.64) * mm, "mid": v(6.97, -0.63) * mm, "end": v(6.96, -0.63) * mm});
            skArc(sketch, "E23.32.3", {"start": v(6.97, -0.64) * mm, "mid": v(6.96, -0.76) * mm, "end": v(6.94, -0.88) * mm});
            skArc(sketch, "E23.32.4", {"start": v(6.94, -0.9) * mm, "mid": v(6.94, -0.89) * mm, "end": v(6.94, -0.88) * mm});
            skArc(sketch, "E23.32.5", {"start": v(6.94, -0.9) * mm, "mid": v(6.69, -0.96) * mm, "end": v(6.43, -1) * mm});
            skArc(sketch, "E23.32.6", {"start": v(6.43, -1) * mm, "mid": v(6.43, -1) * mm, "end": v(6.42, -1) * mm});
            skArc(sketch, "E23.33.0", {"start": v(6.48, 0.53) * mm, "mid": v(6.48, 0.52) * mm, "end": v(6.49, 0.52) * mm});
            skArc(sketch, "E23.33.1", {"start": v(6.98, 0.37) * mm, "mid": v(6.74, 0.46) * mm, "end": v(6.49, 0.52) * mm});
            skArc(sketch, "E23.33.2", {"start": v(7, 0.36) * mm, "mid": v(6.99, 0.37) * mm, "end": v(6.98, 0.37) * mm});
            skArc(sketch, "E23.33.3", {"start": v(7, 0.36) * mm, "mid": v(7, 0.24) * mm, "end": v(7, 0.12) * mm});
            skArc(sketch, "E23.33.4", {"start": v(7, 0.1) * mm, "mid": v(7, 0.11) * mm, "end": v(7, 0.12) * mm});
            skArc(sketch, "E23.33.5", {"start": v(7, 0.1) * mm, "mid": v(6.76, 0) * mm, "end": v(6.5, -0.07) * mm});
            skArc(sketch, "E23.33.6", {"start": v(6.5, -0.07) * mm, "mid": v(6.5, -0.08) * mm, "end": v(6.5, -0.08) * mm});
            skArc(sketch, "E23.34.0", {"start": v(6.34, 1.44) * mm, "mid": v(6.34, 1.44) * mm, "end": v(6.35, 1.43) * mm});
            skArc(sketch, "E23.34.1", {"start": v(6.86, 1.36) * mm, "mid": v(6.6, 1.41) * mm, "end": v(6.35, 1.43) * mm});
            skArc(sketch, "E23.34.2", {"start": v(6.87, 1.35) * mm, "mid": v(6.87, 1.36) * mm, "end": v(6.86, 1.36) * mm});
            skArc(sketch, "E23.34.3", {"start": v(6.87, 1.35) * mm, "mid": v(6.9, 1.23) * mm, "end": v(6.91, 1.11) * mm});
            skArc(sketch, "E23.34.4", {"start": v(6.9, 1.1) * mm, "mid": v(6.91, 1.1) * mm, "end": v(6.91, 1.11) * mm});
            skArc(sketch, "E23.34.5", {"start": v(6.9, 1.1) * mm, "mid": v(6.69, 0.96) * mm, "end": v(6.45, 0.86) * mm});
            skArc(sketch, "E23.34.6", {"start": v(6.45, 0.86) * mm, "mid": v(6.45, 0.85) * mm, "end": v(6.45, 0.84) * mm});
            skArc(sketch, "E23.35.0", {"start": v(6.07, 2.33) * mm, "mid": v(6.07, 2.32) * mm, "end": v(6.08, 2.32) * mm});
            skArc(sketch, "E23.35.1", {"start": v(6.6, 2.32) * mm, "mid": v(6.34, 2.34) * mm, "end": v(6.08, 2.32) * mm});
            skArc(sketch, "E23.35.2", {"start": v(6.6, 2.31) * mm, "mid": v(6.6, 2.32) * mm, "end": v(6.6, 2.32) * mm});
            skArc(sketch, "E23.35.3", {"start": v(6.6, 2.31) * mm, "mid": v(6.65, 2.2) * mm, "end": v(6.68, 2.09) * mm});
            skArc(sketch, "E23.35.4", {"start": v(6.68, 2.07) * mm, "mid": v(6.68, 2.08) * mm, "end": v(6.68, 2.09) * mm});
            skArc(sketch, "E23.35.5", {"start": v(6.68, 2.07) * mm, "mid": v(6.48, 1.9) * mm, "end": v(6.27, 1.77) * mm});
            skArc(sketch, "E23.35.6", {"start": v(6.27, 1.77) * mm, "mid": v(6.26, 1.76) * mm, "end": v(6.26, 1.75) * mm});
            skArc(sketch, "E23.36.0", {"start": v(5.67, 3.17) * mm, "mid": v(5.68, 3.17) * mm, "end": v(5.69, 3.16) * mm});
            skArc(sketch, "E23.36.1", {"start": v(6.2, 3.24) * mm, "mid": v(5.94, 3.22) * mm, "end": v(5.69, 3.16) * mm});
            skArc(sketch, "E23.36.2", {"start": v(6.2, 3.23) * mm, "mid": v(6.2, 3.24) * mm, "end": v(6.2, 3.24) * mm});
            skArc(sketch, "E23.36.3", {"start": v(6.2, 3.23) * mm, "mid": v(6.26, 3.12) * mm, "end": v(6.32, 3.01) * mm});
            skArc(sketch, "E23.36.4", {"start": v(6.32, 3) * mm, "mid": v(6.32, 3) * mm, "end": v(6.32, 3.01) * mm});
            skArc(sketch, "E23.36.5", {"start": v(6.32, 3) * mm, "mid": v(6.14, 2.8) * mm, "end": v(5.95, 2.64) * mm});
            skArc(sketch, "E23.36.6", {"start": v(5.95, 2.64) * mm, "mid": v(5.95, 2.63) * mm, "end": v(5.95, 2.62) * mm});
            skArc(sketch, "E23.37.0", {"start": v(5.16, 3.95) * mm, "mid": v(5.17, 3.94) * mm, "end": v(5.18, 3.94) * mm});
            skArc(sketch, "E23.37.1", {"start": v(5.67, 4.09) * mm, "mid": v(5.42, 4.03) * mm, "end": v(5.18, 3.94) * mm});
            skArc(sketch, "E23.37.2", {"start": v(5.69, 4.08) * mm, "mid": v(5.68, 4.09) * mm, "end": v(5.67, 4.09) * mm});
            skArc(sketch, "E23.37.3", {"start": v(5.69, 4.08) * mm, "mid": v(5.76, 3.98) * mm, "end": v(5.82, 3.88) * mm});
            skArc(sketch, "E23.37.4", {"start": v(5.82, 3.87) * mm, "mid": v(5.83, 3.88) * mm, "end": v(5.82, 3.88) * mm});
            skArc(sketch, "E23.37.5", {"start": v(5.82, 3.87) * mm, "mid": v(5.68, 3.65) * mm, "end": v(5.52, 3.46) * mm});
            skArc(sketch, "E23.37.6", {"start": v(5.52, 3.46) * mm, "mid": v(5.51, 3.45) * mm, "end": v(5.51, 3.44) * mm});
            skArc(sketch, "E23.38.0", {"start": v(4.55, 4.64) * mm, "mid": v(4.56, 4.64) * mm, "end": v(4.57, 4.64) * mm});
            skArc(sketch, "E23.38.1", {"start": v(5.03, 4.85) * mm, "mid": v(4.8, 4.76) * mm, "end": v(4.57, 4.64) * mm});
            skArc(sketch, "E23.38.2", {"start": v(5.05, 4.85) * mm, "mid": v(5.04, 4.85) * mm, "end": v(5.03, 4.85) * mm});
            skArc(sketch, "E23.38.3", {"start": v(5.05, 4.85) * mm, "mid": v(5.13, 4.76) * mm, "end": v(5.21, 4.67) * mm});
            skArc(sketch, "E23.38.4", {"start": v(5.21, 4.66) * mm, "mid": v(5.22, 4.67) * mm, "end": v(5.21, 4.67) * mm});
            skArc(sketch, "E23.38.5", {"start": v(5.21, 4.66) * mm, "mid": v(5.1, 4.43) * mm, "end": v(4.97, 4.2) * mm});
            skArc(sketch, "E23.38.6", {"start": v(4.97, 4.2) * mm, "mid": v(4.96, 4.2) * mm, "end": v(4.97, 4.2) * mm});
            skArc(sketch, "E23.39.0", {"start": v(3.84, 5.24) * mm, "mid": v(3.85, 5.24) * mm, "end": v(3.86, 5.24) * mm});
            skArc(sketch, "E23.39.1", {"start": v(4.3, 5.52) * mm, "mid": v(4.07, 5.4) * mm, "end": v(3.86, 5.24) * mm});
            skArc(sketch, "E23.39.2", {"start": v(4.3, 5.52) * mm, "mid": v(4.3, 5.52) * mm, "end": v(4.3, 5.52) * mm});
            skArc(sketch, "E23.39.3", {"start": v(4.3, 5.52) * mm, "mid": v(4.4, 5.44) * mm, "end": v(4.5, 5.37) * mm});
            skArc(sketch, "E23.39.4", {"start": v(4.5, 5.35) * mm, "mid": v(4.5, 5.36) * mm, "end": v(4.5, 5.37) * mm});
            skArc(sketch, "E23.39.5", {"start": v(4.5, 5.35) * mm, "mid": v(4.42, 5.1) * mm, "end": v(4.32, 4.87) * mm});
            skArc(sketch, "E23.39.6", {"start": v(4.32, 4.87) * mm, "mid": v(4.32, 4.86) * mm, "end": v(4.32, 4.86) * mm});
            skArc(sketch, "E23.40.0", {"start": v(3.06, 5.74) * mm, "mid": v(3.07, 5.73) * mm, "end": v(3.08, 5.74) * mm});
            skArc(sketch, "E23.40.1", {"start": v(3.46, 6.08) * mm, "mid": v(3.26, 5.92) * mm, "end": v(3.08, 5.74) * mm});
            skArc(sketch, "E23.40.2", {"start": v(3.48, 6.08) * mm, "mid": v(3.47, 6.08) * mm, "end": v(3.46, 6.08) * mm});
            skArc(sketch, "E23.40.3", {"start": v(3.48, 6.08) * mm, "mid": v(3.58, 6.01) * mm, "end": v(3.68, 5.95) * mm});
            skArc(sketch, "E23.40.4", {"start": v(3.7, 5.94) * mm, "mid": v(3.69, 5.95) * mm, "end": v(3.68, 5.95) * mm});
            skArc(sketch, "E23.40.5", {"start": v(3.7, 5.94) * mm, "mid": v(3.65, 5.69) * mm, "end": v(3.58, 5.44) * mm});
            skArc(sketch, "E23.40.6", {"start": v(3.58, 5.44) * mm, "mid": v(3.58, 5.43) * mm, "end": v(3.58, 5.42) * mm});
            skArc(sketch, "E23.41.0", {"start": v(2.21, 6.11) * mm, "mid": v(2.22, 6.11) * mm, "end": v(2.23, 6.12) * mm});
            skArc(sketch, "E23.41.1", {"start": v(2.56, 6.5) * mm, "mid": v(2.38, 6.32) * mm, "end": v(2.23, 6.12) * mm});
            skArc(sketch, "E23.41.2", {"start": v(2.58, 6.5) * mm, "mid": v(2.57, 6.5) * mm, "end": v(2.56, 6.5) * mm});
            skArc(sketch, "E23.41.3", {"start": v(2.58, 6.5) * mm, "mid": v(2.69, 6.46) * mm, "end": v(2.8, 6.42) * mm});
            skArc(sketch, "E23.41.4", {"start": v(2.8, 6.4) * mm, "mid": v(2.8, 6.41) * mm, "end": v(2.8, 6.42) * mm});
            skArc(sketch, "E23.41.5", {"start": v(2.8, 6.4) * mm, "mid": v(2.8, 6.15) * mm, "end": v(2.77, 5.9) * mm});
            skArc(sketch, "E23.41.6", {"start": v(2.77, 5.9) * mm, "mid": v(2.77, 5.88) * mm, "end": v(2.78, 5.88) * mm});
            skArc(sketch, "E23.42.0", {"start": v(1.32, 6.36) * mm, "mid": v(1.33, 6.37) * mm, "end": v(1.33, 6.37) * mm});
            skArc(sketch, "E23.42.1", {"start": v(1.61, 6.8) * mm, "mid": v(1.46, 6.6) * mm, "end": v(1.33, 6.37) * mm});
            skArc(sketch, "E23.42.2", {"start": v(1.62, 6.8) * mm, "mid": v(1.62, 6.8) * mm, "end": v(1.61, 6.8) * mm});
            skArc(sketch, "E23.42.3", {"start": v(1.62, 6.8) * mm, "mid": v(1.74, 6.78) * mm, "end": v(1.86, 6.75) * mm});
            skArc(sketch, "E23.42.4", {"start": v(1.87, 6.74) * mm, "mid": v(1.86, 6.74) * mm, "end": v(1.86, 6.75) * mm});
            skArc(sketch, "E23.42.5", {"start": v(1.87, 6.74) * mm, "mid": v(1.9, 6.48) * mm, "end": v(1.9, 6.23) * mm});
            skArc(sketch, "E23.42.6", {"start": v(1.9, 6.23) * mm, "mid": v(1.9, 6.22) * mm, "end": v(1.91, 6.21) * mm});
            skArc(sketch, "E23.43.0", {"start": v(0.4, 6.49) * mm, "mid": v(0.4, 6.5) * mm, "end": v(0.41, 6.5) * mm});
            skArc(sketch, "E23.43.1", {"start": v(0.63, 6.96) * mm, "mid": v(0.5, 6.74) * mm, "end": v(0.41, 6.5) * mm});
            skArc(sketch, "E23.43.2", {"start": v(0.64, 6.97) * mm, "mid": v(0.63, 6.97) * mm, "end": v(0.63, 6.96) * mm});
            skArc(sketch, "E23.43.3", {"start": v(0.64, 6.97) * mm, "mid": v(0.76, 6.96) * mm, "end": v(0.88, 6.94) * mm});
            skArc(sketch, "E23.43.4", {"start": v(0.9, 6.94) * mm, "mid": v(0.89, 6.94) * mm, "end": v(0.88, 6.94) * mm});
            skArc(sketch, "E23.43.5", {"start": v(0.9, 6.94) * mm, "mid": v(0.96, 6.69) * mm, "end": v(1, 6.43) * mm});
            skArc(sketch, "E23.43.6", {"start": v(1, 6.43) * mm, "mid": v(1, 6.43) * mm, "end": v(1, 6.42) * mm});
            skSolve(sketch);
        }
        {
            var Q0;
            Q0=qSketchRegion(id+"F4",true);
            extrude(context, id + "F5", {"entities" : qUnion([Q0]), "operationType" : NewBodyOperationType.REMOVE, "endBound" : BoundingType.THROUGH_ALL, "oppositeDirection" : true, "depth" : 25 * mm});
        }
    });
